# Revit family: LIPROOF103
name_source: partatom
category: Lighting Fixtures
units: mm (PartAtom-declared; Revit-internal decimal feet)

## family parameters
Cut with Voids When Loaded = No
Host = Face
Light Source = Yes
Maintain Annotation Orientation = Yes
Part Type = Normal
Room Calculation Point = No
Round Connector Dimension = Use Diameter
Shared = No

## types (1)
- LIPROOF103
    Color Filter = 16777215
    Default Elevation = 1219 mm
    Dimming Lamp Color Temperature Shift = <None>
    Emit from Line Length = 610 mm
    LuxLight_Alto = 0 mm  [stored 0 ft]
    LuxLight_AltoAreaLuminosa = 0 mm  [stored 0 ft]
    LuxLight_Amperios = 0
    LuxLight_Ancho = 0 mm  [stored 0 ft]
    LuxLight_AnchoAreaLuminosa = 0 mm  [stored 0 ft]
    LuxLight_Diametro = 0 mm  [stored 0 ft]
    LuxLight_DiametroAreaLuminosa = 0 mm  [stored 0 ft]
    LuxLight_Largo = 1200 mm
    LuxLight_LargoAreaLuminosa = 0 mm  [stored 0 ft]
    LuxLight_Lumenes = 5900 lm
    LuxLight_ProtuberanciaTecho = 0 mm  [stored 0 ft]
    LuxLight_Temperatura = 0 K
    LuxLight_Watios = 40 W
    Manufacturer = LUXLIGHT
    Photometric Web File = LIPROOF103 36W 4000K .ies
    Tilt Angle = 0.00°

note: [stored X ft] marks values corroborated as IEEE doubles in the binary element streams (Revit-internal decimal feet)

## geometry (parser evidence)
native form markers: Sweep x9
no freeform markers — native parametric forms only
